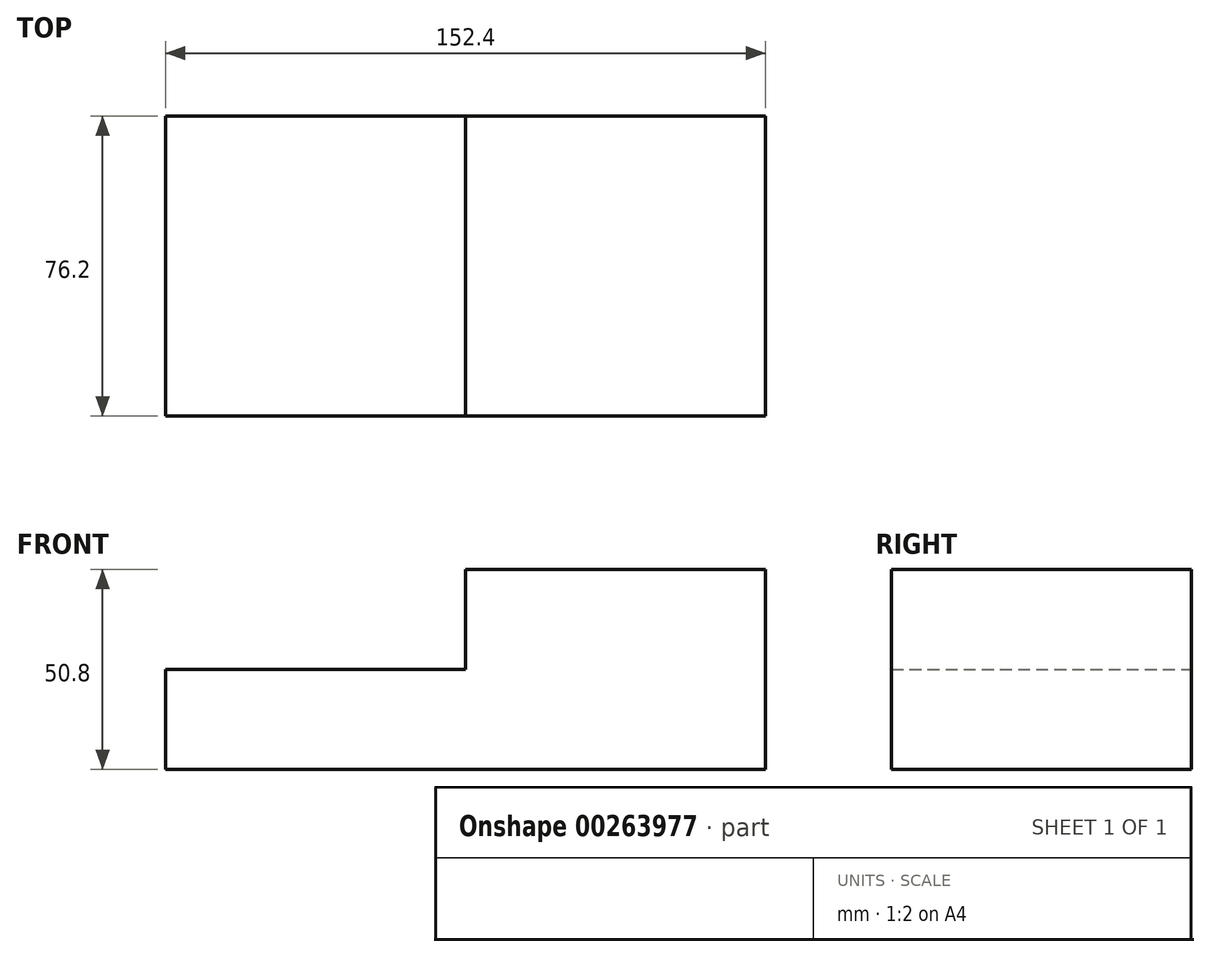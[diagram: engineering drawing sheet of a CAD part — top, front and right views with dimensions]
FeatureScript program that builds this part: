
annotation { "Feature Type Name" : "Feature", "Feature Type Description" : "" }
export const myFeature = defineFeature(function(context is Context, id is Id, definition is map)
    precondition{}
    {
        {
            var Q0;
            Q0=qCreatedBy(makeId("Front.planeOp"),FACE);
            var sketch = newSketch(context, id + "F0", { "sketchPlane" : qUnion([Q0])});
            skLineSegment(sketch, "E0", {"start": v(0, 0) * mm, "end": v(152.4, 0) * mm});
            skLineSegment(sketch, "E1", {"start": v(152.4, 0) * mm, "end": v(152.4, 50.8) * mm});
            skLineSegment(sketch, "E2", {"start": v(152.4, 50.8) * mm, "end": v(76.2, 50.8) * mm});
            skLineSegment(sketch, "E3", {"start": v(76.2, 50.8) * mm, "end": v(76.2, 25.4) * mm});
            skLineSegment(sketch, "E4", {"start": v(76.2, 25.4) * mm, "end": v(0, 25.4) * mm});
            skLineSegment(sketch, "E5", {"start": v(0, 25.4) * mm, "end": v(0, 0) * mm});
            skSolve(sketch);
        }
        {
            var Q0;
            Q0 = qSketchRegion(id + "F0", true);
            extrude(context, id + "F1", {"entities" : qUnion([Q0]), "depth" : 76.2 * mm});
        }
    });
